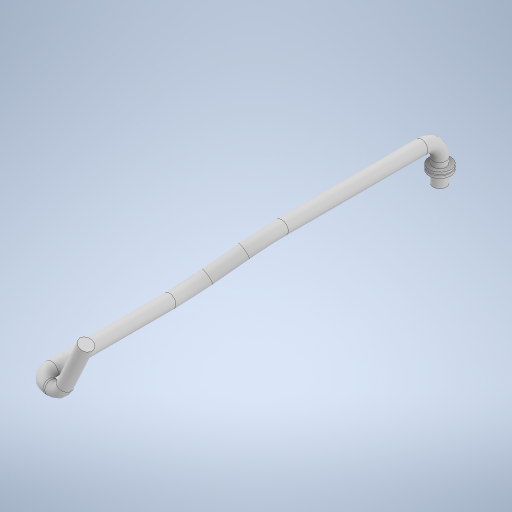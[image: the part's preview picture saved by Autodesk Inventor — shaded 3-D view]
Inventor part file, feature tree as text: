
AUTODESK INVENTOR PART (.ipt)
format: ipt  version: 2023 (Build 270158000, 158)  size: 1,733,120 bytes
history: native  units: in
note: dims shown in document units (in); Inventor stores cm internally (conversion verified against a paired STEP export)
features: sketch x3, other x2, plane x2, sweep x1, revolve x1, mirror x1
ambient origin geometry x8: Origin, YZ Plane, XZ Plane, XY Plane, X Axis, Y Axis, Z Axis, Center Point
bodies: Solid1 (feature_tree)
feature tree (10):
  other  "s282_locomotive_body"
  sketch  "3D Sketch1"
  plane  "Work Plane1"
  sweep  "Sweep1"
  plane  "Work Plane3"
  revolve  "Revolution1"  [1 undecoded]
  mirror  "Mirror1"
  sketch  "Sketch1"  dims[d0=0.0in d1=0.0in d2=6.5in]
  sketch  "Sketch4"  dims[d10=1.1811in d11=1.1811in d12=0.3937in d13=90.0deg d14=36.0in d15=36.0in d16=9.0in d17=8.0in d32=8.0in]
  other  "s282_locomotive_body_0"
note: 1 required parameter value undecoded (feature->parameter linkage not recoverable at this tier; creation-order binding heuristic only, values carry confidence <= 0.55)
